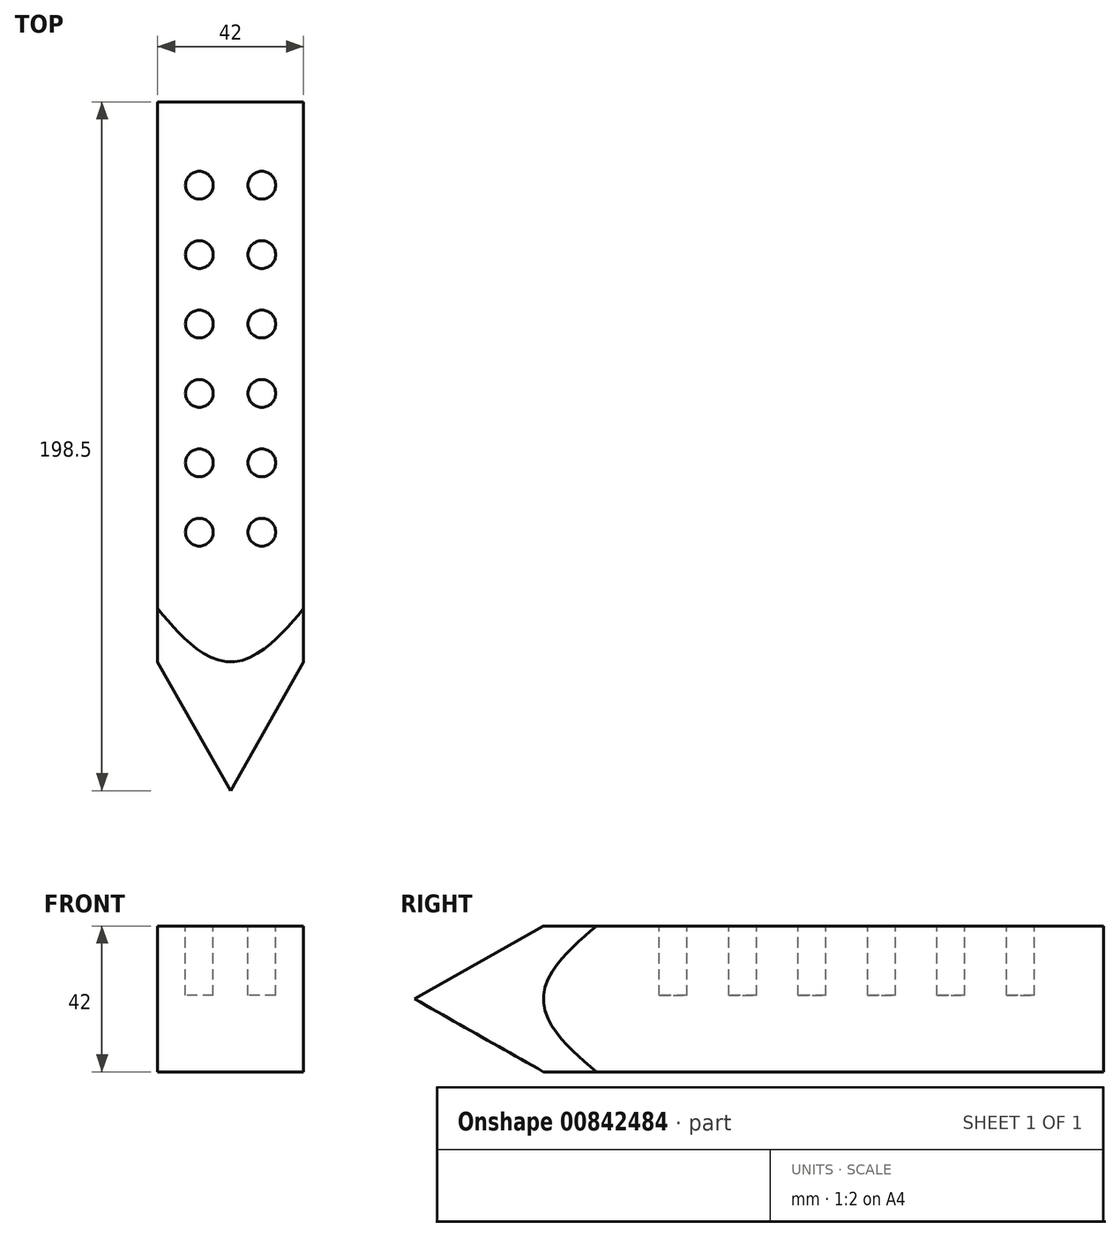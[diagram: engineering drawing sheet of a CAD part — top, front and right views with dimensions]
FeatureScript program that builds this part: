
annotation { "Feature Type Name" : "Feature", "Feature Type Description" : "" }
export const myFeature = defineFeature(function(context is Context, id is Id, definition is map)
    precondition{}
    {
        {
            var Q0;
            Q0=qCreatedBy(makeId("Front.planeOp"),FACE);
            var sketch = newSketch(context, id + "F0", { "sketchPlane" : qUnion([Q0])});
            skCircle(sketch, "E0.cCircle", {"center": v(0, 0) * mm, "radius": 21 * mm, "construction": true});
            skLineSegment(sketch, "E0.0", {"start": v(-21, 21) * mm, "end": v(21, 21) * mm});
            skLineSegment(sketch, "E0.1", {"start": v(21, 21) * mm, "end": v(21, -21) * mm});
            skLineSegment(sketch, "E0.2", {"start": v(21, -21) * mm, "end": v(-21, -21) * mm});
            skLineSegment(sketch, "E0.3", {"start": v(-21, -21) * mm, "end": v(-21, 21) * mm});
            skPoint(sketch, "E0.0.midPoint", {"position": v(0, 21) * mm});
            skSolve(sketch);
        }
        {
            var Q0;
            Q0 = qSketchRegion(id + "F0", true);
            extrude(context, id + "F1", {"entities" : qUnion([Q0]), "depth" : 146 * mm, "offsetDistance" : 25 * mm});
        }
        {
            var Q0;
            Q0=makeQuery(id+"F1.opExtrude","CAP_FACE",FACE,{"disambiguationData":[OSD([sQuery(id+"F0.wireOp",EDGE,"E0.0"),sQuery(id+"F0.wireOp",EDGE,"E0.1"),sQuery(id+"F0.wireOp",EDGE,"E0.2"),sQuery(id+"F0.wireOp",EDGE,"E0.3")])],"isStart":false});
            var sketch = newSketch(context, id + "F2", { "sketchPlane" : qUnion([Q0])});
            skCircle(sketch, "E1", {"center": v(0, 0) * mm, "radius": 29.7 * mm});
            skSolve(sketch);
        }
        {
            var Q0;
            Q0 = qSketchRegion(id + "F2", true);
            extrude(context, id + "F3", {"entities" : qUnion([Q0]), "operationType" : NewBodyOperationType.ADD, "depth" : 52.5 * mm, "offsetDistance" : 25 * mm, "hasDraft" : true, "draftAngle" : 29.5 * degree, "draftPullDirection" : true});
        }
        {
            var Q0;
            Q0=makeQuery(id+"F1.opExtrude","SWEPT_FACE",FACE,{"disambiguationData":[OSD([sQuery(id+"F0.wireOp",EDGE,"E0.3")])]});
            var sketch = newSketch(context, id + "F4", { "sketchPlane" : qUnion([Q0])});
            skCircle(sketch, "E2", {"center": v(146, 0) * mm, "radius": 21 * mm});
            skSolve(sketch);
        }
        {
            var Q0;
            Q0 = qSketchRegion(id + "F4", true);
            extrude(context, id + "F5", {"entities" : qUnion([Q0]), "operationType" : NewBodyOperationType.REMOVE, "depth" : 25 * mm, "offsetDistance" : 25 * mm});
        }
        {
            var Q0;
            Q0=makeQuery(id+"F1.opExtrude","SWEPT_FACE",FACE,{"disambiguationData":[OSD([sQuery(id+"F0.wireOp",EDGE,"E0.0")])]});
            var sketch = newSketch(context, id + "F6", { "sketchPlane" : qUnion([Q0])});
            skCircle(sketch, "E3", {"center": v(0, -146) * mm, "radius": 21 * mm});
            skSolve(sketch);
        }
        {
            var Q0;
            Q0=makeQuery(id+"F1.opExtrude","SWEPT_FACE",FACE,{"disambiguationData":[OSD([sQuery(id+"F0.wireOp",EDGE,"E0.1")])]});
            var sketch = newSketch(context, id + "F7", { "sketchPlane" : qUnion([Q0])});
            skCircle(sketch, "E4", {"center": v(-146, 0) * mm, "radius": 21 * mm});
            skSolve(sketch);
        }
        {
            var Q0;
            Q0=makeQuery(id+"F1.opExtrude","SWEPT_FACE",FACE,{"disambiguationData":[OSD([sQuery(id+"F0.wireOp",EDGE,"E0.2")])]});
            var sketch = newSketch(context, id + "F8", { "sketchPlane" : qUnion([Q0])});
            skCircle(sketch, "E5", {"center": v(0, 146) * mm, "radius": 21 * mm});
            skSolve(sketch);
        }
        {
            var Q0;
            Q0 = qSketchRegion(id + "F6", true);
            extrude(context, id + "F9", {"entities" : qUnion([Q0]), "operationType" : NewBodyOperationType.REMOVE, "depth" : 25 * mm, "offsetDistance" : 25 * mm});
        }
        {
            var Q0;
            Q0 = qSketchRegion(id + "F7", true);
            extrude(context, id + "F10", {"entities" : qUnion([Q0]), "operationType" : NewBodyOperationType.REMOVE, "depth" : 25 * mm, "offsetDistance" : 25 * mm});
        }
        {
            var Q0;
            Q0 = qSketchRegion(id + "F8", true);
            extrude(context, id + "F11", {"entities" : qUnion([Q0]), "operationType" : NewBodyOperationType.REMOVE, "depth" : 25 * mm, "offsetDistance" : 25 * mm});
        }
        {
            var Q0;
            Q0=makeQuery(id+"F9.boolean.opBoolean","MERGE",FACE,{"derivedFrom":[makeQuery(id+"F1.opExtrude","SWEPT_FACE",FACE,{"disambiguationData":[OSD([sQuery(id+"F0.wireOp",EDGE,"E0.0")])]}),makeQuery(id+"F9.opExtrude","CAP_FACE",FACE,{"disambiguationData":[OSD([sQuery(id+"F6.wireOp",EDGE,"E3")])],"isStart":true})]});
            var sketch = newSketch(context, id + "F12", { "sketchPlane" : qUnion([Q0])});
            skCircle(sketch, "E6", {"center": v(-9, -24) * mm, "radius": 4 * mm});
            skCircle(sketch, "E7.0.1.0", {"center": v(-9, -44) * mm, "radius": 4 * mm});
            skCircle(sketch, "E7.0.2.0", {"center": v(-9, -64) * mm, "radius": 4 * mm});
            skCircle(sketch, "E7.0.3.0", {"center": v(-9, -84) * mm, "radius": 4 * mm});
            skCircle(sketch, "E7.0.4.0", {"center": v(-9, -104) * mm, "radius": 4 * mm});
            skCircle(sketch, "E7.0.5.0", {"center": v(-9, -124) * mm, "radius": 4 * mm});
            skCircle(sketch, "E7.1.0.0", {"center": v(9, -24) * mm, "radius": 4 * mm});
            skCircle(sketch, "E7.1.1.0", {"center": v(9, -44) * mm, "radius": 4 * mm});
            skCircle(sketch, "E7.1.2.0", {"center": v(9, -64) * mm, "radius": 4 * mm});
            skCircle(sketch, "E7.1.3.0", {"center": v(9, -84) * mm, "radius": 4 * mm});
            skCircle(sketch, "E7.1.4.0", {"center": v(9, -104) * mm, "radius": 4 * mm});
            skCircle(sketch, "E7.1.5.0", {"center": v(9, -124) * mm, "radius": 4 * mm});
            skLineSegment(sketch, "E7.direction1", {"start": v(-9, -24) * mm, "end": v(9, -24) * mm, "construction": true});
            skLineSegment(sketch, "E7.direction2", {"start": v(-9, -24) * mm, "end": v(-9, -44) * mm, "construction": true});
            skSolve(sketch);
        }
        {
            var Q0;
            Q0 = qSketchRegion(id + "F12", true);
            extrude(context, id + "F13", {"entities" : qUnion([Q0]), "operationType" : NewBodyOperationType.REMOVE, "oppositeDirection" : true, "depth" : 20 * mm, "offsetDistance" : 25 * mm});
        }
    });
